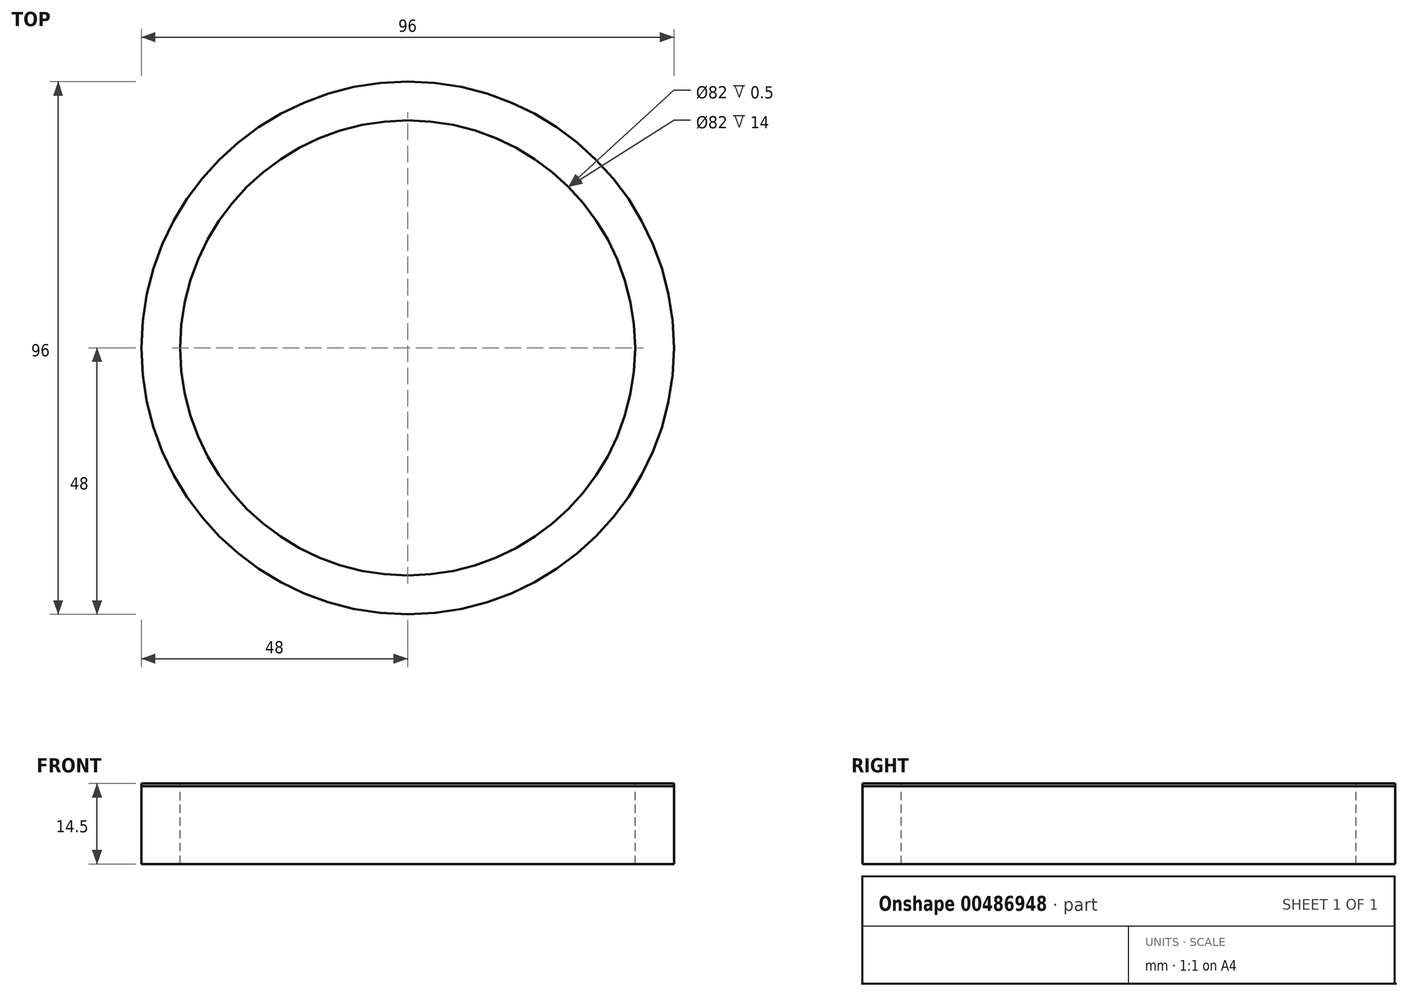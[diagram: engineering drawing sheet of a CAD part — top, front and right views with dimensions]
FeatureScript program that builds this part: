
annotation { "Feature Type Name" : "Feature", "Feature Type Description" : "" }
export const myFeature = defineFeature(function(context is Context, id is Id, definition is map)
    precondition{}
    {
        {
            var Q0;
            Q0=qCreatedBy(makeId("Top.planeOp"),FACE);
            var sketch = newSketch(context, id + "F0", { "sketchPlane" : qUnion([Q0])});
            skCircle(sketch, "E0", {"center": v(0, 0) * mm, "radius": 41 * mm});
            skCircle(sketch, "E1", {"center": v(0, 0) * mm, "radius": 48 * mm});
            skSolve(sketch);
        }
        {
            var Q0;
            Q0=makeQuery(id+"F0.imprint","IMPRINT",FACE,{"disambiguationData":[TD([[makeQuery(id+"F0.imprint","IMPRINT",EDGE,{"derivedFrom":sQuery(id+"F0.wireOp",EDGE,"E0")}),-1.0]])]});
            extrude(context, id + "F1", {"entities" : qUnion([Q0]), "oppositeDirection" : true, "depth" : 14 * mm});
        }
        {
            var Q0;
            Q0=makeQuery(id+"F1.opExtrude","CAP_FACE",FACE,{"disambiguationData":[OSD([sQuery(id+"F0.wireOp",EDGE,"E0"),sQuery(id+"F0.wireOp",EDGE,"E1")])],"isStart":true});
            extrude(context, id + "F2", {"entities" : qUnion([Q0]), "depth" : 0.5 * mm});
        }
    });
